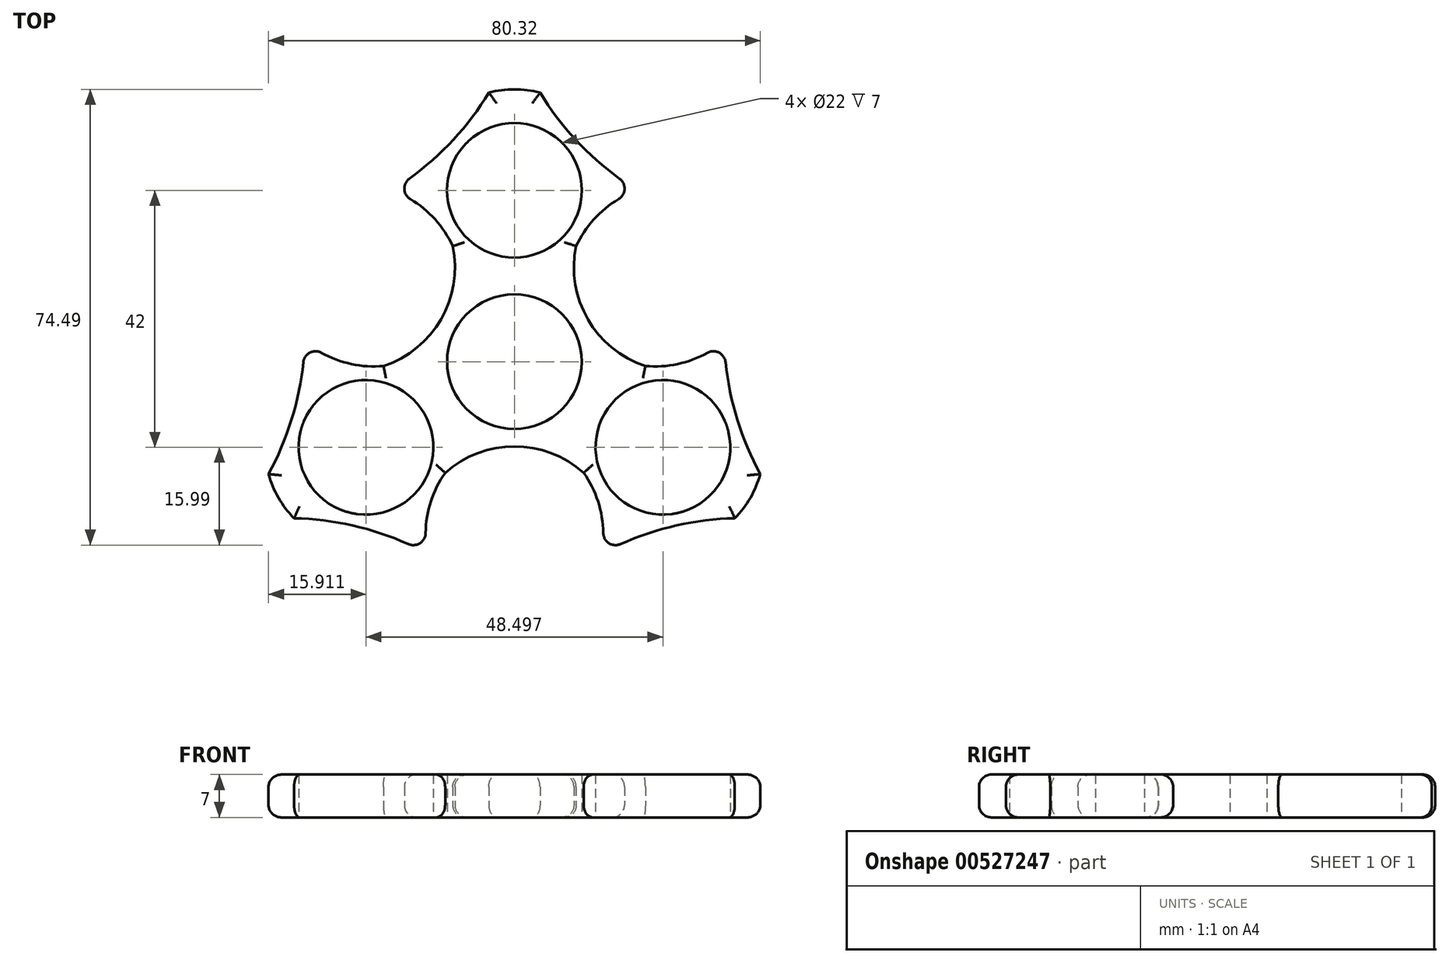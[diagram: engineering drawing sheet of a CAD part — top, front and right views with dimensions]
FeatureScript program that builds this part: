
annotation { "Feature Type Name" : "Feature", "Feature Type Description" : "" }
export const myFeature = defineFeature(function(context is Context, id is Id, definition is map)
    precondition{}
    {
        {
            var Q0;
            Q0=qCreatedBy(makeId("Top.planeOp"),FACE);
            var sketch = newSketch(context, id + "F0", { "sketchPlane" : qUnion([Q0])});
            skCircle(sketch, "E0", {"center": v(0, 0) * mm, "radius": 11 * mm});
            skCircle(sketch, "E1", {"center": v(0, 28) * mm, "radius": 11 * mm});
            skPoint(sketch, "E2.orphan", {"position": v(0, 48) * mm});
            skPoint(sketch, "E3.orphan", {"position": v(-11, 0) * mm});
            skArc(sketch, "E4.3", {"start": v(4.18, 43.96) * mm, "mid": v(0, 44.5) * mm, "end": v(-4.18, 43.96) * mm});
            skArc(sketch, "E5", {"start": v(-20, 28) * mm, "mid": v(-11.15, 35.05) * mm, "end": v(-4.18, 43.96) * mm});
            skArc(sketch, "E6.MirrorCS", {"start": v(20, 28) * mm, "mid": v(11.15, 35.05) * mm, "end": v(4.18, 43.96) * mm});
            skArc(sketch, "E7.1.0", {"start": v(-13.46, -20.47) * mm, "mid": v(-13.76, -22.27) * mm, "end": v(-14, -24.08) * mm});
            skArc(sketch, "E7.1.1", {"start": v(-14.25, -31.32) * mm, "mid": v(-24.78, -27.19) * mm, "end": v(-35.99, -25.6) * mm});
            skArc(sketch, "E7.1.2", {"start": v(-40.16, -18.37) * mm, "mid": v(-38.54, -22.25) * mm, "end": v(-35.99, -25.6) * mm});
            skArc(sketch, "E7.1.3", {"start": v(-34.25, 3.32) * mm, "mid": v(-35.93, -7.87) * mm, "end": v(-40.16, -18.37) * mm});
            skCircle(sketch, "E7.1.5", {"center": v(-24.25, -14) * mm, "radius": 11 * mm});
            skArc(sketch, "E7.2.0", {"start": v(24.46, -1.42) * mm, "mid": v(26.17, -0.78) * mm, "end": v(27.86, -0.08) * mm});
            skArc(sketch, "E7.2.1", {"start": v(34.25, 3.32) * mm, "mid": v(35.93, -7.87) * mm, "end": v(40.16, -18.37) * mm});
            skArc(sketch, "E7.2.2", {"start": v(35.99, -25.6) * mm, "mid": v(38.54, -22.25) * mm, "end": v(40.16, -18.37) * mm});
            skArc(sketch, "E7.2.3", {"start": v(14.25, -31.32) * mm, "mid": v(24.78, -27.19) * mm, "end": v(35.99, -25.6) * mm});
            skCircle(sketch, "E7.2.5", {"center": v(24.25, -14) * mm, "radius": 11 * mm});
            skArc(sketch, "E8", {"start": v(-24.46, -1.42) * mm, "mid": v(-12.84, 5.6) * mm, "end": v(-10.07, 18.88) * mm});
            skArc(sketch, "E9", {"start": v(-10.07, 18.88) * mm, "mid": v(-14.13, 24.42) * mm, "end": v(-20, 28) * mm});
            skPoint(sketch, "E10.orphan", {"position": v(-11, 21.89) * mm});
            skArc(sketch, "E11.MirrorCS", {"start": v(10.07, 18.88) * mm, "mid": v(14.13, 24.42) * mm, "end": v(20, 28) * mm});
            skArc(sketch, "E12.1.0", {"start": v(-11.31, -18.16) * mm, "mid": v(-14.09, -24.45) * mm, "end": v(-14.25, -31.32) * mm});
            skArc(sketch, "E12.1.1", {"start": v(-21.39, -0.72) * mm, "mid": v(-28.22, 0.03) * mm, "end": v(-34.25, 3.32) * mm});
            skArc(sketch, "E12.1.2", {"start": v(11.31, -18.16) * mm, "mid": v(0, -13.84) * mm, "end": v(-11.31, -18.16) * mm});
            skArc(sketch, "E12.2.0", {"start": v(21.39, -0.72) * mm, "mid": v(28.22, 0.03) * mm, "end": v(34.25, 3.32) * mm});
            skArc(sketch, "E12.2.1", {"start": v(11.31, -18.16) * mm, "mid": v(14.09, -24.45) * mm, "end": v(14.25, -31.32) * mm});
            skArc(sketch, "E12.2.2", {"start": v(10.07, 18.88) * mm, "mid": v(11.99, 6.92) * mm, "end": v(21.39, -0.72) * mm});
            skPoint(sketch, "E13.orphan", {"position": v(11, 21.89) * mm});
            skPoint(sketch, "E14.orphan", {"position": v(34.25, 3.32) * mm});
            skPoint(sketch, "E15.orphan", {"position": v(-14.25, -31.32) * mm});
            skPoint(sketch, "E16.orphan", {"position": v(14.25, -31.32) * mm});
            skPoint(sketch, "E17.orphan", {"position": v(13.46, -20.47) * mm});
            skSolve(sketch);
        }
        {
            var Q0;
            Q0=makeQuery(id+"F0.imprint","IMPRINT",FACE,{"disambiguationData":[TD([[makeQuery(id+"F0.imprint","IMPRINT",EDGE,{"derivedFrom":sQuery(id+"F0.wireOp",EDGE,"E0")}),-1.0]])]});
            extrude(context, id + "F1", {"entities" : qUnion([Q0]), "endBound" : BoundingType.SYMMETRIC, "depth" : 7 * mm, "offsetDistance" : 25 * mm});
        }
        {
            var Q0;
            Q0=makeQuery(id+"F1.opExtrude","CAP_EDGE",EDGE,{"disambiguationData":[OSD([sQuery(id+"F0.wireOp",EDGE,"E12.1.2")])],"isStart":false});
            var Q1;
            Q1=makeQuery(id+"F1.opExtrude","CAP_EDGE",EDGE,{"disambiguationData":[OSD([sQuery(id+"F0.wireOp",EDGE,"E12.1.0")])],"isStart":false});
            var Q2;
            Q2=makeQuery(id+"F1.opExtrude","CAP_EDGE",EDGE,{"disambiguationData":[OSD([sQuery(id+"F0.wireOp",EDGE,"E7.1.1")])],"isStart":false});
            var Q3;
            Q3=makeQuery(id+"F1.opExtrude","CAP_EDGE",EDGE,{"disambiguationData":[OSD([sQuery(id+"F0.wireOp",EDGE,"E7.1.2")])],"isStart":false});
            var Q4;
            Q4=makeQuery(id+"F1.opExtrude","CAP_EDGE",EDGE,{"disambiguationData":[OSD([sQuery(id+"F0.wireOp",EDGE,"E7.1.3")])],"isStart":false});
            var Q5;
            Q5=makeQuery(id+"F1.opExtrude","CAP_EDGE",EDGE,{"disambiguationData":[OSD([sQuery(id+"F0.wireOp",EDGE,"E12.1.1")])],"isStart":false});
            var Q6;
            Q6=makeQuery(id+"F1.opExtrude","CAP_EDGE",EDGE,{"disambiguationData":[OSD([sQuery(id+"F0.wireOp",EDGE,"E8")])],"isStart":false});
            var Q7;
            Q7=makeQuery(id+"F1.opExtrude","CAP_EDGE",EDGE,{"disambiguationData":[OSD([sQuery(id+"F0.wireOp",EDGE,"E9")])],"isStart":false});
            var Q8;
            Q8=makeQuery(id+"F1.opExtrude","CAP_EDGE",EDGE,{"disambiguationData":[OSD([sQuery(id+"F0.wireOp",EDGE,"E5")])],"isStart":false});
            var Q9;
            Q9=makeQuery(id+"F1.opExtrude","CAP_EDGE",EDGE,{"disambiguationData":[OSD([sQuery(id+"F0.wireOp",EDGE,"E4.3")])],"isStart":false});
            var Q10;
            Q10=makeQuery(id+"F1.opExtrude","CAP_EDGE",EDGE,{"disambiguationData":[OSD([sQuery(id+"F0.wireOp",EDGE,"E6.MirrorCS")])],"isStart":false});
            var Q11;
            Q11=makeQuery(id+"F1.opExtrude","CAP_EDGE",EDGE,{"disambiguationData":[OSD([sQuery(id+"F0.wireOp",EDGE,"E11.MirrorCS")])],"isStart":false});
            var Q12;
            Q12=makeQuery(id+"F1.opExtrude","CAP_EDGE",EDGE,{"disambiguationData":[OSD([sQuery(id+"F0.wireOp",EDGE,"E12.2.2")])],"isStart":false});
            var Q13;
            Q13=makeQuery(id+"F1.opExtrude","CAP_EDGE",EDGE,{"disambiguationData":[OSD([sQuery(id+"F0.wireOp",EDGE,"E12.2.0")])],"isStart":false});
            var Q14;
            Q14=makeQuery(id+"F1.opExtrude","CAP_EDGE",EDGE,{"disambiguationData":[OSD([sQuery(id+"F0.wireOp",EDGE,"E7.2.1")])],"isStart":false});
            var Q15;
            Q15=makeQuery(id+"F1.opExtrude","CAP_EDGE",EDGE,{"disambiguationData":[OSD([sQuery(id+"F0.wireOp",EDGE,"E7.2.2")])],"isStart":false});
            var Q16;
            Q16=makeQuery(id+"F1.opExtrude","CAP_EDGE",EDGE,{"disambiguationData":[OSD([sQuery(id+"F0.wireOp",EDGE,"E7.2.3")])],"isStart":false});
            var Q17;
            Q17=makeQuery(id+"F1.opExtrude","CAP_EDGE",EDGE,{"disambiguationData":[OSD([sQuery(id+"F0.wireOp",EDGE,"E12.2.1")])],"isStart":false});
            var Q18;
            Q18=makeQuery(id+"F1.opExtrude","CAP_EDGE",EDGE,{"disambiguationData":[OSD([sQuery(id+"F0.wireOp",EDGE,"E12.1.2")])],"isStart":true});
            var Q19;
            Q19=makeQuery(id+"F1.opExtrude","CAP_EDGE",EDGE,{"disambiguationData":[OSD([sQuery(id+"F0.wireOp",EDGE,"E12.2.1")])],"isStart":true});
            var Q20;
            Q20=makeQuery(id+"F1.opExtrude","CAP_EDGE",EDGE,{"disambiguationData":[OSD([sQuery(id+"F0.wireOp",EDGE,"E7.2.3")])],"isStart":true});
            var Q21;
            Q21=makeQuery(id+"F1.opExtrude","CAP_EDGE",EDGE,{"disambiguationData":[OSD([sQuery(id+"F0.wireOp",EDGE,"E7.2.2")])],"isStart":true});
            var Q22;
            Q22=makeQuery(id+"F1.opExtrude","CAP_EDGE",EDGE,{"disambiguationData":[OSD([sQuery(id+"F0.wireOp",EDGE,"E7.2.1")])],"isStart":true});
            var Q23;
            Q23=makeQuery(id+"F1.opExtrude","CAP_EDGE",EDGE,{"disambiguationData":[OSD([sQuery(id+"F0.wireOp",EDGE,"E12.2.0")])],"isStart":true});
            var Q24;
            Q24=makeQuery(id+"F1.opExtrude","CAP_EDGE",EDGE,{"disambiguationData":[OSD([sQuery(id+"F0.wireOp",EDGE,"E12.2.2")])],"isStart":true});
            var Q25;
            Q25=makeQuery(id+"F1.opExtrude","CAP_EDGE",EDGE,{"disambiguationData":[OSD([sQuery(id+"F0.wireOp",EDGE,"E11.MirrorCS")])],"isStart":true});
            var Q26;
            Q26=makeQuery(id+"F1.opExtrude","CAP_EDGE",EDGE,{"disambiguationData":[OSD([sQuery(id+"F0.wireOp",EDGE,"E6.MirrorCS")])],"isStart":true});
            var Q27;
            Q27=makeQuery(id+"F1.opExtrude","CAP_EDGE",EDGE,{"disambiguationData":[OSD([sQuery(id+"F0.wireOp",EDGE,"E4.3")])],"isStart":true});
            var Q28;
            Q28=makeQuery(id+"F1.opExtrude","CAP_EDGE",EDGE,{"disambiguationData":[OSD([sQuery(id+"F0.wireOp",EDGE,"E5")])],"isStart":true});
            var Q29;
            Q29=makeQuery(id+"F1.opExtrude","CAP_EDGE",EDGE,{"disambiguationData":[OSD([sQuery(id+"F0.wireOp",EDGE,"E9")])],"isStart":true});
            var Q30;
            Q30=makeQuery(id+"F1.opExtrude","CAP_EDGE",EDGE,{"disambiguationData":[OSD([sQuery(id+"F0.wireOp",EDGE,"E8")])],"isStart":true});
            var Q31;
            Q31=makeQuery(id+"F1.opExtrude","CAP_EDGE",EDGE,{"disambiguationData":[OSD([sQuery(id+"F0.wireOp",EDGE,"E12.1.1")])],"isStart":true});
            var Q32;
            Q32=makeQuery(id+"F1.opExtrude","CAP_EDGE",EDGE,{"disambiguationData":[OSD([sQuery(id+"F0.wireOp",EDGE,"E7.1.3")])],"isStart":true});
            var Q33;
            Q33=makeQuery(id+"F1.opExtrude","CAP_EDGE",EDGE,{"disambiguationData":[OSD([sQuery(id+"F0.wireOp",EDGE,"E7.1.2")])],"isStart":true});
            var Q34;
            Q34=makeQuery(id+"F1.opExtrude","CAP_EDGE",EDGE,{"disambiguationData":[OSD([sQuery(id+"F0.wireOp",EDGE,"E7.1.1")])],"isStart":true});
            var Q35;
            Q35=makeQuery(id+"F1.opExtrude","CAP_EDGE",EDGE,{"disambiguationData":[OSD([sQuery(id+"F0.wireOp",EDGE,"E12.1.0")])],"isStart":true});
            var Q36;
            Q36=makeQuery(id+"F1.opExtrude","SWEPT_EDGE",EDGE,{"disambiguationData":[OSD([sQuery(id+"F0.wireOp",EDGE,"E7.2.3"),sQuery(id+"F0.wireOp",EDGE,"E12.2.1")])]});
            var Q37;
            Q37=makeQuery(id+"F1.opExtrude","SWEPT_EDGE",EDGE,{"disambiguationData":[OSD([sQuery(id+"F0.wireOp",EDGE,"E7.1.1"),sQuery(id+"F0.wireOp",EDGE,"E12.1.0")])]});
            var Q38;
            Q38=makeQuery(id+"F1.opExtrude","SWEPT_EDGE",EDGE,{"disambiguationData":[OSD([sQuery(id+"F0.wireOp",EDGE,"E7.2.1"),sQuery(id+"F0.wireOp",EDGE,"E12.2.0")])]});
            var Q39;
            Q39=makeQuery(id+"F1.opExtrude","SWEPT_EDGE",EDGE,{"disambiguationData":[OSD([sQuery(id+"F0.wireOp",EDGE,"E6.MirrorCS"),sQuery(id+"F0.wireOp",EDGE,"E11.MirrorCS")])]});
            var Q40;
            Q40=makeQuery(id+"F1.opExtrude","SWEPT_EDGE",EDGE,{"disambiguationData":[OSD([sQuery(id+"F0.wireOp",EDGE,"E5"),sQuery(id+"F0.wireOp",EDGE,"E9")])]});
            var Q41;
            Q41=makeQuery(id+"F1.opExtrude","SWEPT_EDGE",EDGE,{"disambiguationData":[OSD([sQuery(id+"F0.wireOp",EDGE,"E7.1.3"),sQuery(id+"F0.wireOp",EDGE,"E12.1.1")])]});
            fillet(context, id + "F2", {"entities" : qUnion([Q0, Q1, Q2, Q3, Q4, Q5, Q6, Q7, Q8, Q9, Q10, Q11, Q12, Q13, Q14, Q15, Q16, Q17, Q18, Q19, Q20, Q21, Q22, Q23, Q24, Q25, Q26, Q27, Q28, Q29, Q30, Q31, Q32, Q33, Q34, Q35, Q36, Q37, Q38, Q39, Q40, Q41]), "radius" : 2 * mm, "tangentPropagation" : true, "allowEdgeOverflow" : false});
        }
    });
